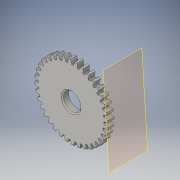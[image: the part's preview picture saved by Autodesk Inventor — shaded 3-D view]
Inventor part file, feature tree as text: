
AUTODESK INVENTOR PART (.ipt)
format: ipt  version: 2016 (Build 200138000, 138)  size: 940,544 bytes
history: native  units: in
note: dims shown in document units (in); Inventor stores cm internally (conversion verified against a paired STEP export)
features: plane x1, extrude x1, sketch x1, chamfer x1
ambient origin geometry x8: Origin, YZ Plane, XZ Plane, XY Plane, X Axis, Y Axis, Z Axis, Center Point
bodies: Solid1 (feature_tree)
feature tree (4):
  plane  "Work Plane1"
  extrude  "Extrusion1"  [1 undecoded]
  sketch  "Sketch3"  dims[d0=1.0in d1=0.0in]
  chamfer  "Chamfer1"  [1 undecoded]
note: 2 required parameter values undecoded (feature->parameter linkage not recoverable at this tier; creation-order binding heuristic only, values carry confidence <= 0.55)
